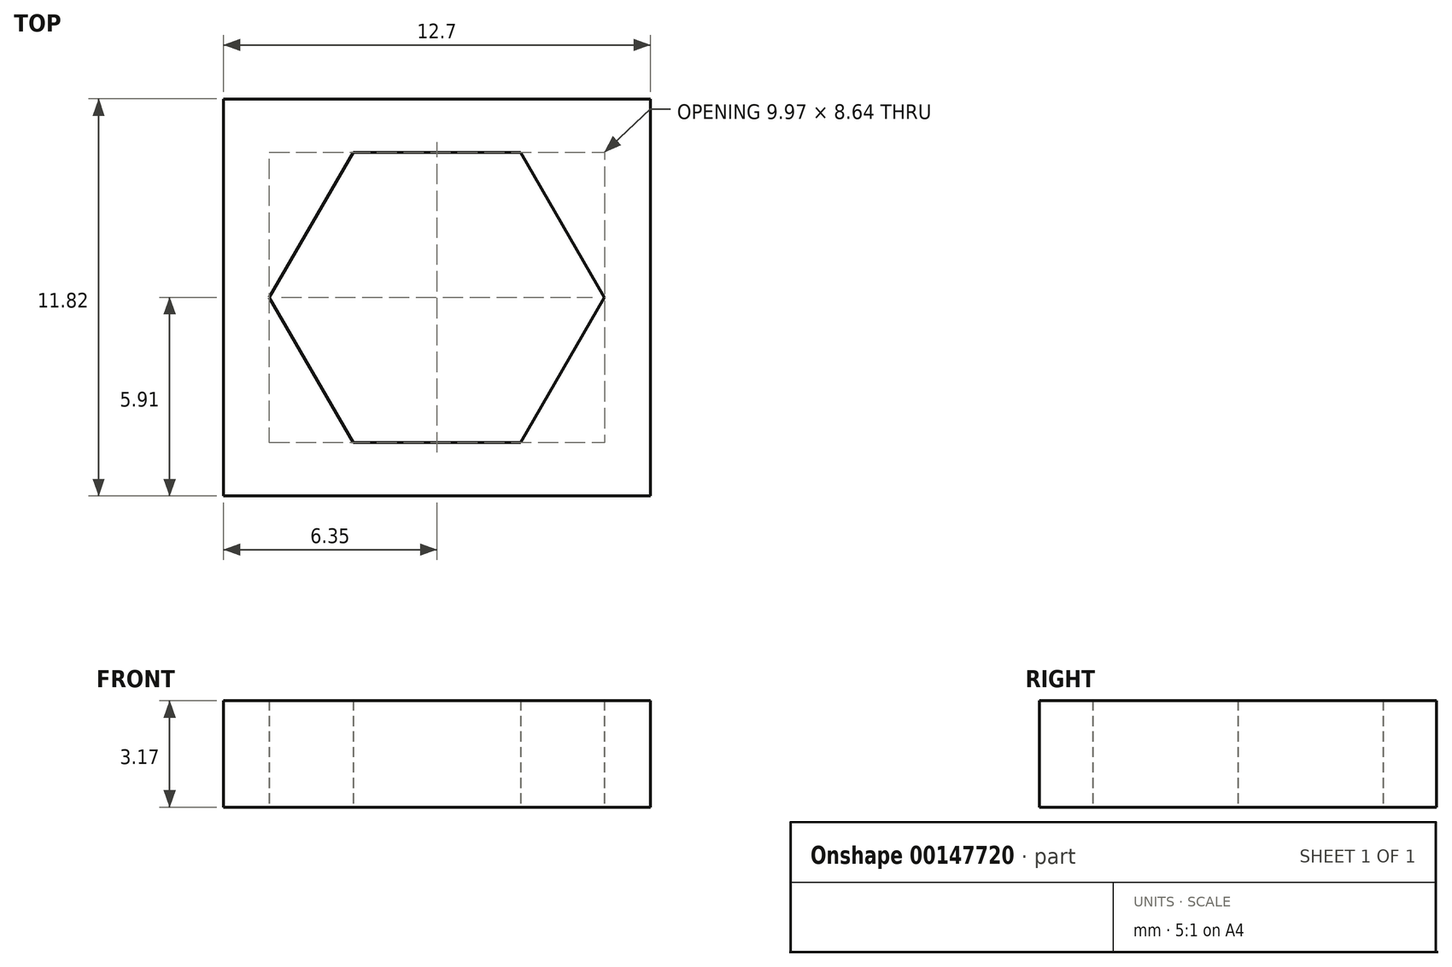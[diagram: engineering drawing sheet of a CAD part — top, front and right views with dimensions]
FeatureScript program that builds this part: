
annotation { "Feature Type Name" : "Feature", "Feature Type Description" : "" }
export const myFeature = defineFeature(function(context is Context, id is Id, definition is map)
    precondition{}
    {
        {
            var Q0;
            Q0=qCreatedBy(makeId("Top.planeOp"),FACE);
            var sketch = newSketch(context, id + "F0", { "sketchPlane" : qUnion([Q0])});
            skCircle(sketch, "E0.cCircle", {"center": v(0, 0) * mm, "radius": 4.32 * mm, "construction": true});
            skLineSegment(sketch, "E0.0", {"start": v(2.5, -4.32) * mm, "end": v(-2.5, -4.32) * mm});
            skLineSegment(sketch, "E0.1", {"start": v(-2.5, -4.32) * mm, "end": v(-4.99, 0) * mm});
            skLineSegment(sketch, "E0.2", {"start": v(-4.99, 0) * mm, "end": v(-2.5, 4.32) * mm});
            skLineSegment(sketch, "E0.3", {"start": v(-2.5, 4.32) * mm, "end": v(2.5, 4.32) * mm});
            skLineSegment(sketch, "E0.4", {"start": v(2.5, 4.32) * mm, "end": v(4.99, 0) * mm});
            skLineSegment(sketch, "E0.5", {"start": v(4.99, 0) * mm, "end": v(2.5, -4.32) * mm});
            skPoint(sketch, "E0.0.midPoint", {"position": v(0, -4.32) * mm});
            skLineSegment(sketch, "E1.bottom", {"start": v(6.35, -5.9) * mm, "end": v(-6.35, -5.9) * mm});
            skLineSegment(sketch, "E1.top", {"start": v(6.35, 5.9) * mm, "end": v(-6.35, 5.9) * mm});
            skLineSegment(sketch, "E1.left", {"start": v(6.35, -5.9) * mm, "end": v(6.35, 5.9) * mm});
            skLineSegment(sketch, "E1.right", {"start": v(-6.35, -5.9) * mm, "end": v(-6.35, 5.9) * mm});
            skSolve(sketch);
        }
        {
            var Q0;
            Q0=qSketchRegion(id+"F0",true);
            extrude(context, id + "F1", {"entities" : qUnion([Q0]), "depth" : 3.17 * mm});
        }
    });
